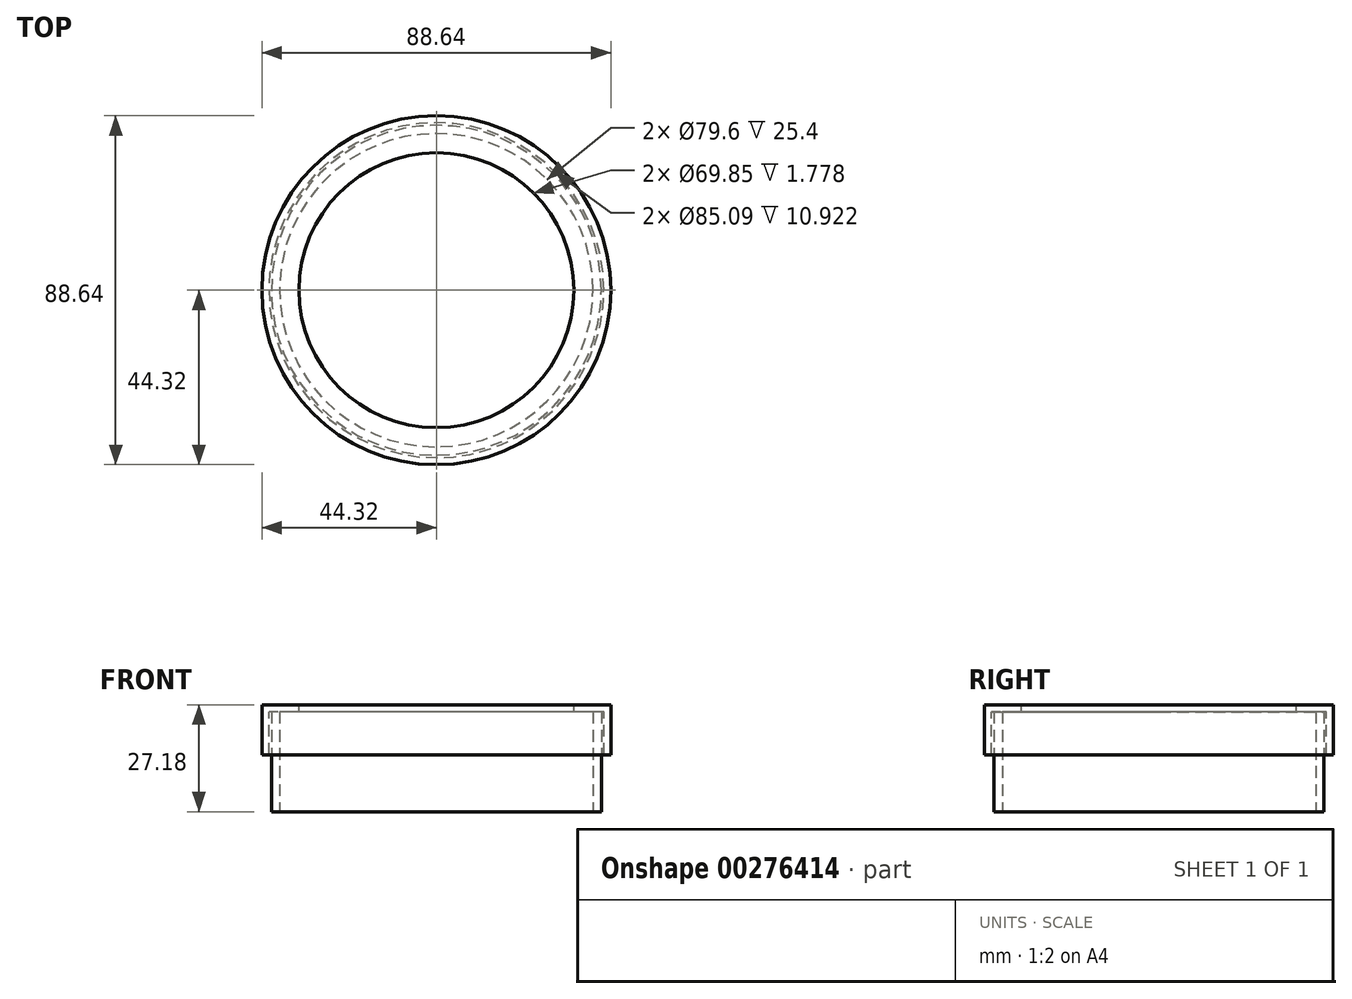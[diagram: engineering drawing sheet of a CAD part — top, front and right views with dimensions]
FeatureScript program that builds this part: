
annotation { "Feature Type Name" : "Feature", "Feature Type Description" : "" }
export const myFeature = defineFeature(function(context is Context, id is Id, definition is map)
    precondition{}
    {
        {
            var Q0;
            Q0=qCreatedBy(makeId("Top.planeOp"),FACE);
            var sketch = newSketch(context, id + "F0", { "sketchPlane" : qUnion([Q0])});
            skCircle(sketch, "E0", {"center": v(0, 0) * mm, "radius": 41.91 * mm});
            skCircle(sketch, "E1", {"center": v(0, 0) * mm, "radius": 39.8 * mm});
            skSolve(sketch);
        }
        {
            var Q0;
            Q0 = qSketchRegion(id + "F0", true);
            extrude(context, id + "F1", {"entities" : qUnion([Q0]), "endBound" : BoundingType.SYMMETRIC, "depth" : 25.4 * mm});
        }
        {
            var Q0;
            Q0=qCreatedBy(makeId("Front.planeOp"),FACE);
            var sketch = newSketch(context, id + "F2", { "sketchPlane" : qUnion([Q0])});
            skLineSegment(sketch, "E2", {"start": v(0, 15.3) * mm, "end": v(0, -14.93) * mm, "construction": true});
            skLineSegment(sketch, "E3", {"start": v(34.93, 14.48) * mm, "end": v(34.93, 12.7) * mm});
            skLineSegment(sketch, "E4", {"start": v(34.93, 12.7) * mm, "end": v(42.55, 12.7) * mm});
            skLineSegment(sketch, "E5", {"start": v(42.55, 12.7) * mm, "end": v(42.55, 1.78) * mm});
            skLineSegment(sketch, "E6", {"start": v(42.55, 1.78) * mm, "end": v(44.32, 1.78) * mm});
            skLineSegment(sketch, "E7", {"start": v(44.32, 1.78) * mm, "end": v(44.32, 14.48) * mm});
            skLineSegment(sketch, "E8", {"start": v(44.32, 14.48) * mm, "end": v(34.93, 14.48) * mm});
            skSolve(sketch);
        }
        {
            var Q0;
            Q0 = qSketchRegion(id + "F2", true);
            var Q1;
            Q1=sQuery(id+"F2.wireOp",EDGE,"E2");
            revolve(context, id + "F3", {"operationType" : NewBodyOperationType.ADD, "entities" : qUnion([Q0]), "axis" : qUnion([Q1]), "revolveType" : RevolveType.FULL});
        }
        {
            var Q0;
            Q0=makeQuery(id+"F1.opExtrude","SWEPT_BODY",BODY,{"disambiguationData":[OSD([sQuery(id+"F0.wireOp",EDGE,"E0"),sQuery(id+"F0.wireOp",EDGE,"E1")])]});
            transform(context, id + "F4", {"entities" : qUnion([Q0]), "transformType" : TransformType.TRANSLATION_3D, "dx" : 0 * mm, "dy" : 0 * mm, "dz" : 0 * mm, "makeCopy" : true});
        }
    });
